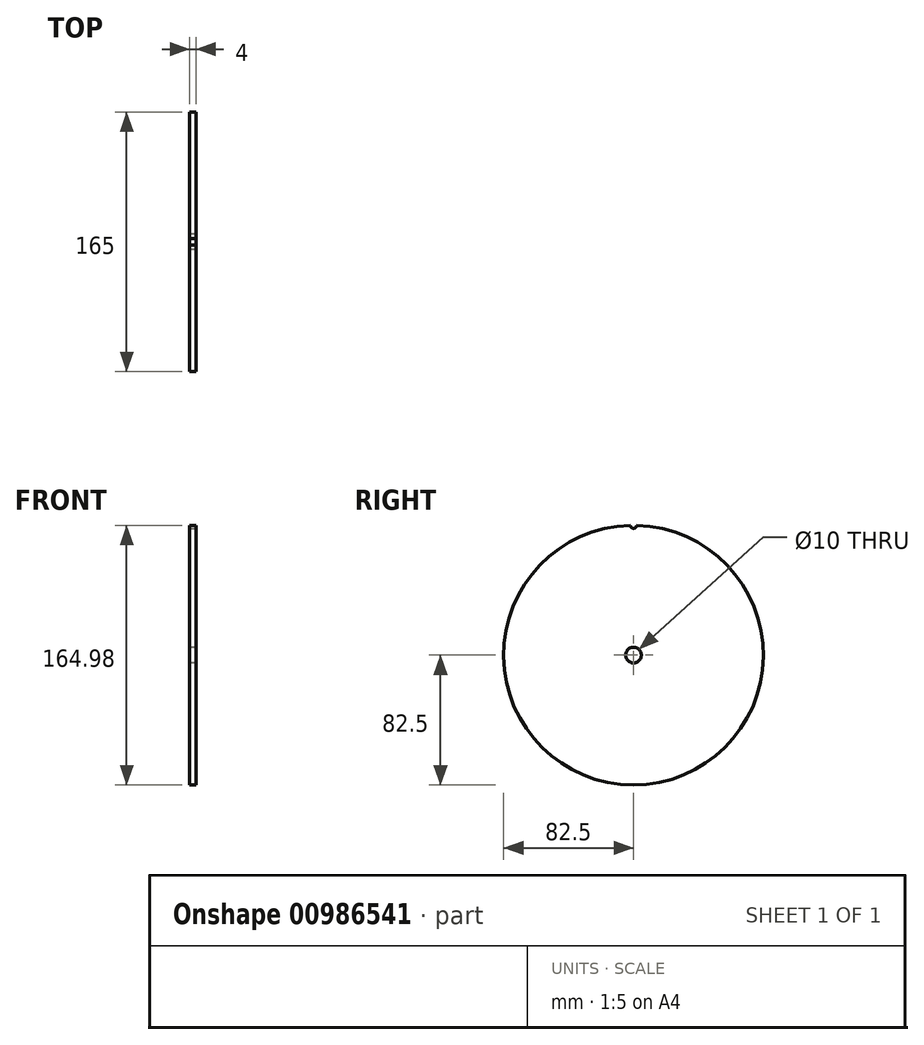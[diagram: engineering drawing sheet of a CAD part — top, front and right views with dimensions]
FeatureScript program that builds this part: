
annotation { "Feature Type Name" : "Feature", "Feature Type Description" : "" }
export const myFeature = defineFeature(function(context is Context, id is Id, definition is map)
    precondition{}
    {
        {
            var Q0;
            Q0=qCreatedBy(makeId("Right.planeOp"),FACE);
            var sketch = newSketch(context, id + "F0", { "sketchPlane" : qUnion([Q0])});
            skCircle(sketch, "E0", {"center": v(0, 0) * mm, "radius": 82.5 * mm});
            skCircle(sketch, "E1", {"center": v(0, 0) * mm, "radius": 5 * mm});
            skSolve(sketch);
        }
        {
            var Q0;
            Q0 = qSketchRegion(id + "F0", true);
            extrude(context, id + "F1", {"entities" : qUnion([Q0]), "depth" : 2 * mm, "offsetDistance" : 25 * mm, "hasSecondDirection" : true, "secondDirectionOppositeDirection" : true, "secondDirectionDepth" : 2 * mm});
        }
        {
            var Q0;
            Q0=makeQuery(id+"F1.opExtrude","CAP_FACE",FACE,{"disambiguationData":[OSD([sQuery(id+"F0.wireOp",EDGE,"E0")])],"isStart":false});
            var sketch = newSketch(context, id + "F2", { "sketchPlane" : qUnion([Q0])});
            skCircle(sketch, "E2", {"center": v(0, 82.5) * mm, "radius": 2 * mm});
            skSolve(sketch);
        }
        {
            var Q0;
            Q0 = qSketchRegion(id + "F2", true);
            extrude(context, id + "F3", {"entities" : qUnion([Q0]), "operationType" : NewBodyOperationType.REMOVE, "endBound" : BoundingType.THROUGH_ALL, "oppositeDirection" : true, "depth" : 25 * mm, "offsetDistance" : 25 * mm});
        }
    });
